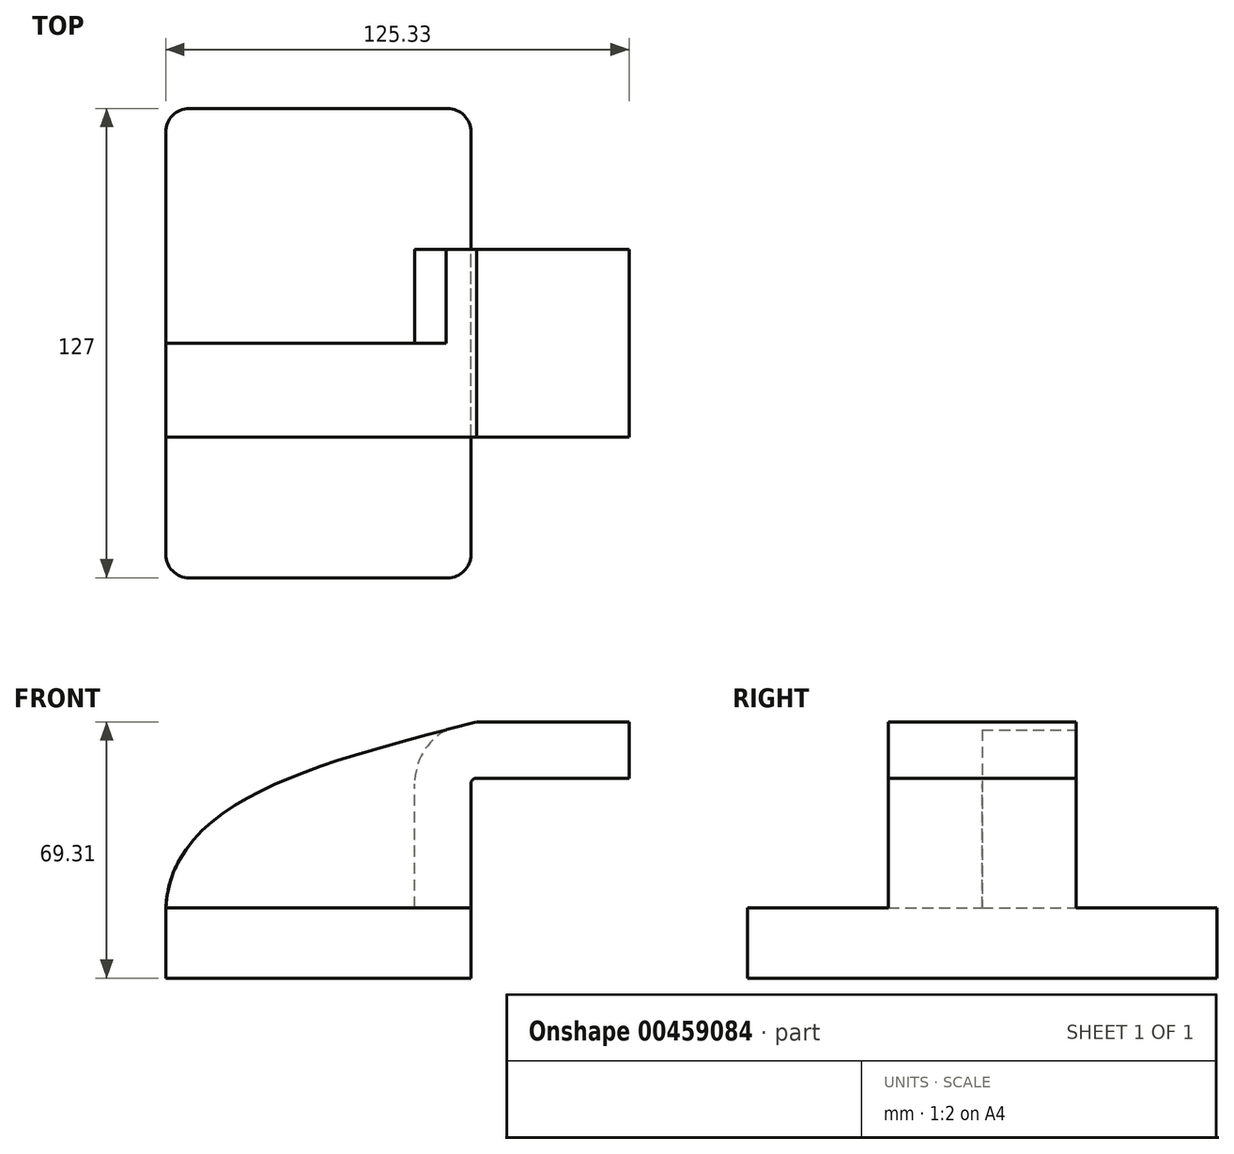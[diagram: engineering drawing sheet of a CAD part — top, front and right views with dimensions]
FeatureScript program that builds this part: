
annotation { "Feature Type Name" : "Feature", "Feature Type Description" : "" }
export const myFeature = defineFeature(function(context is Context, id is Id, definition is map)
    precondition{}
    {
        {
            var Q0;
            Q0=qCreatedBy(makeId("Front.planeOp"),FACE);
            var sketch = newSketch(context, id + "F0", { "sketchPlane" : qUnion([Q0])});
            skLineSegment(sketch, "E0.bottom", {"start": v(41.27, 9.53) * mm, "end": v(-41.28, 9.53) * mm});
            skLineSegment(sketch, "E0.top", {"start": v(41.28, -9.52) * mm, "end": v(-41.27, -9.52) * mm});
            skLineSegment(sketch, "E0.left", {"start": v(41.28, 9.53) * mm, "end": v(41.28, -9.52) * mm});
            skLineSegment(sketch, "E0.right", {"start": v(-41.28, 9.53) * mm, "end": v(-41.27, -9.52) * mm});
            skPoint(sketch, "E0.middle", {"position": v(0, 0) * mm});
            skLineSegment(sketch, "E1.bottom", {"start": v(109.45, 33.67) * mm, "end": v(58.65, 33.67) * mm});
            skLineSegment(sketch, "E1.top", {"start": v(109.45, 62.25) * mm, "end": v(58.65, 62.25) * mm});
            skLineSegment(sketch, "E1.left", {"start": v(109.45, 33.67) * mm, "end": v(109.45, 62.25) * mm});
            skLineSegment(sketch, "E1.right", {"start": v(58.65, 33.67) * mm, "end": v(58.65, 62.25) * mm});
            skPoint(sketch, "E1.middle", {"position": v(84.05, 47.96) * mm});
            skLineSegment(sketch, "E2", {"start": v(41.27, 9.53) * mm, "end": v(41.27, 43.05) * mm});
            skArc(sketch, "E3", {"start": v(41.27, 43.05) * mm, "mid": v(41.71, 44.1) * mm, "end": v(42.76, 44.54) * mm});
            skLineSegment(sketch, "E4", {"start": v(42.76, 44.54) * mm, "end": v(84.05, 44.54) * mm});
            skPoint(sketch, "E4.endSnap0", {"position": v(84.05, 33.67) * mm});
            skLineSegment(sketch, "E5.0", {"start": v(42.76, 59.78) * mm, "end": v(84.05, 59.78) * mm});
            skArc(sketch, "E5.1", {"start": v(26.03, 43.05) * mm, "mid": v(30.93, 54.88) * mm, "end": v(42.76, 59.78) * mm});
            skLineSegment(sketch, "E5.2", {"start": v(26.03, 9.53) * mm, "end": v(26.03, 43.05) * mm});
            skLineSegment(sketch, "E6", {"start": v(84.05, 59.78) * mm, "end": v(84.05, 44.54) * mm});
            skFitSpline(sketch, "E7", {"points": [v(42.76, 59.78) * mm, v(-41.28, 9.53) * mm], "startDerivative": vector(-128.1, -33.31) * mm, "endDerivative": vector(-4.76, -88.35) * mm});
            skSolve(sketch);
        }
        {
            var Q0;
            Q0=makeQuery(id+"F0.imprint","IMPRINT",FACE,{"disambiguationData":[TD([[makeQuery(id+"F0.imprint","IMPRINT",EDGE,{"derivedFrom":sQuery(id+"F0.wireOp",EDGE,"E0.top")}),-1.0]])]});
            extrude(context, id + "F1", {"entities" : qUnion([Q0]), "depth" : 127 * mm, "symmetric" : true});
        }
        {
            var Q0;
            {var subQ1=sQuery(id+"F0.wireOp",EDGE,"E2");Q0=makeQuery(id+"F0.imprint","IMPRINT",FACE,{"disambiguationData":[TD([[makeQuery(id+"F0.imprint","IMPRINT",EDGE,{"derivedFrom":subQ1}),1.0]])]});}
            var Q1;
            {var subQ5=sQuery(id+"F0.wireOp",EDGE,"E6");Q1=makeQuery(id+"F0.imprint","IMPRINT",FACE,{"disambiguationData":[TD([[makeQuery(id+"F0.imprint","IMPRINT",EDGE,{"derivedFrom":subQ5}),-1.0]])]});}
            extrude(context, id + "F2", {"entities" : qUnion([Q0, Q1]), "operationType" : NewBodyOperationType.ADD, "depth" : 50.8 * mm, "symmetric" : true});
        }
        {
            var Q0;
            {var subQ3=sQuery(id+"F0.wireOp",EDGE,"E5.2");Q0=makeQuery(id+"F0.imprint","IMPRINT",FACE,{"disambiguationData":[TD([[makeQuery(id+"F0.imprint","IMPRINT",EDGE,{"derivedFrom":subQ3}),1.0]])]});}
            extrude(context, id + "F3", {"entities" : qUnion([Q0]), "operationType" : NewBodyOperationType.ADD, "depth" : 25.4 * mm});
        }
        {
            var Q0;
            Q0=makeQuery(id+"F1.opExtrude","CAP_EDGE",EDGE,{"disambiguationData":[OSD([sQuery(id+"F0.wireOp",EDGE,"E0.left")])],"isStart":false});
            var Q1;
            Q1=makeQuery(id+"F1.opExtrude","CAP_EDGE",EDGE,{"disambiguationData":[OSD([sQuery(id+"F0.wireOp",EDGE,"E0.right")])],"isStart":false});
            var Q2;
            Q2=makeQuery(id+"F1.opExtrude","CAP_EDGE",EDGE,{"disambiguationData":[OSD([sQuery(id+"F0.wireOp",EDGE,"E0.left")])],"isStart":true});
            var Q3;
            Q3=makeQuery(id+"F1.opExtrude","CAP_EDGE",EDGE,{"disambiguationData":[OSD([sQuery(id+"F0.wireOp",EDGE,"E0.right")])],"isStart":true});
            fillet(context, id + "F4", {"entities" : qUnion([Q0, Q1, Q2, Q3]), "radius" : 6.35 * mm, "tangentPropagation" : true, "allowEdgeOverflow" : false});
        }
    });
